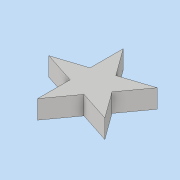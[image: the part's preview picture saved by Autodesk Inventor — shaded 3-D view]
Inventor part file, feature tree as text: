
AUTODESK INVENTOR PART (.ipt)
format: ipt  version: 2019 (Build 230136000, 136)  size: 92,672 bytes
history: native  units: mm
features: other x1, extrude x1, sketch x1
ambient origin geometry x8: Origin, YZ Plane, XZ Plane, XY Plane, X Axis, Y Axis, Z Axis, Center Point
bodies: Body1 (feature_tree)
feature tree (3):
  other  "Твердое тело1"
  extrude  "Выдавливание1"  Depth=172.0mm
  sketch  "Эскиз1"
